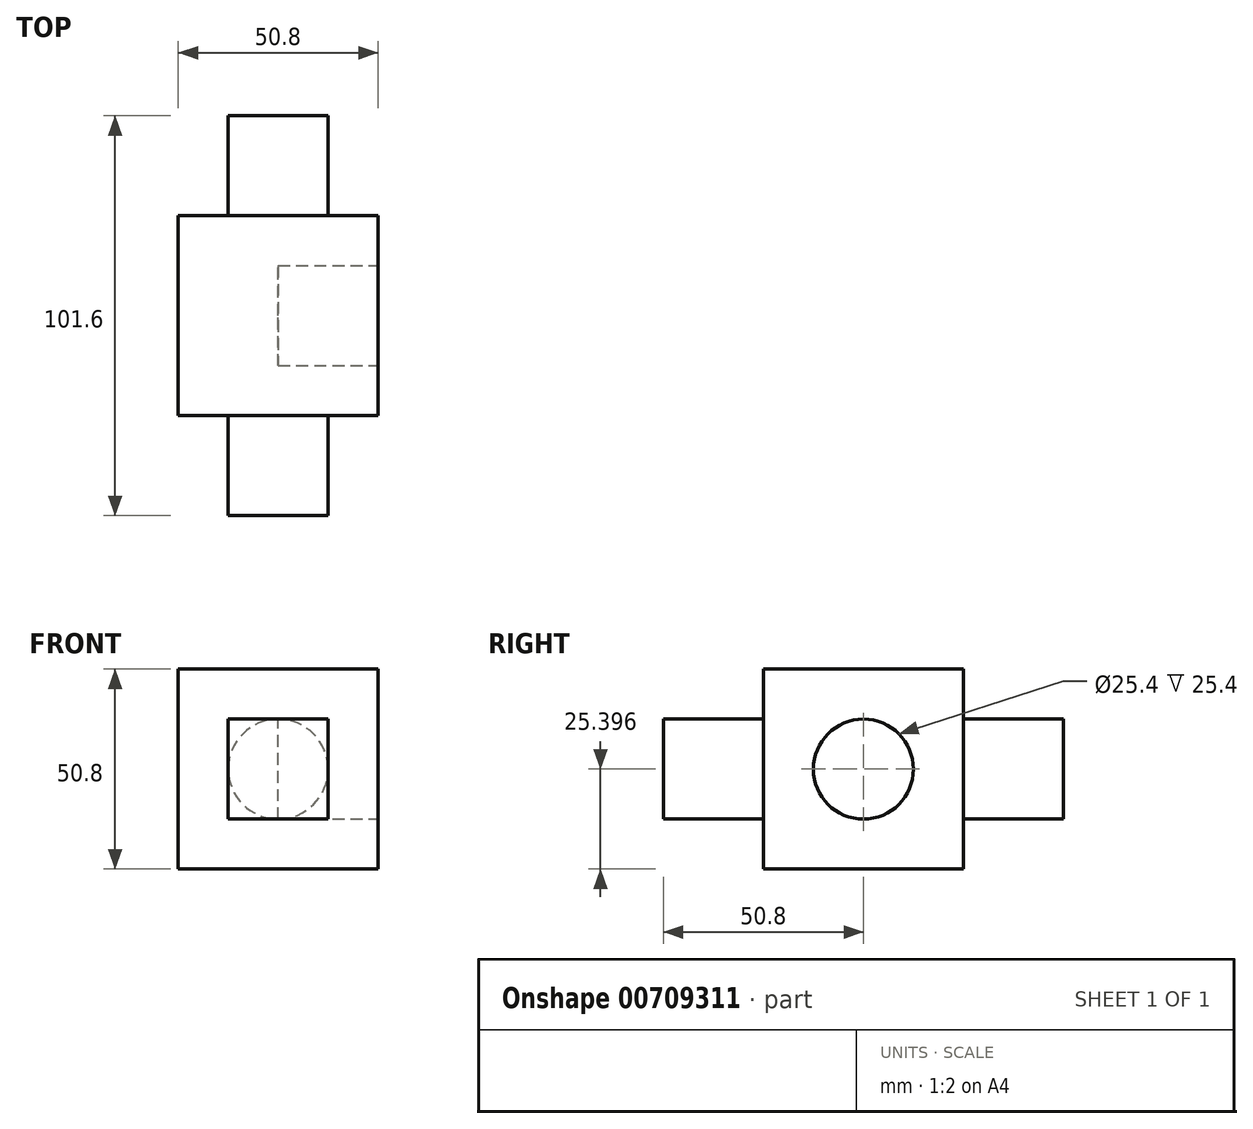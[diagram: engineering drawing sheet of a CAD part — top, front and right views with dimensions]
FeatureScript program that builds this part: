
annotation { "Feature Type Name" : "Feature", "Feature Type Description" : "" }
export const myFeature = defineFeature(function(context is Context, id is Id, definition is map)
    precondition{}
    {
        {
            var Q0;
            Q0=qCreatedBy(makeId("Front.planeOp"),FACE);
            var sketch = newSketch(context, id + "F0", { "sketchPlane" : qUnion([Q0])});
            skLineSegment(sketch, "E0.bottom", {"start": v(-56.81, 48.29) * mm, "end": v(-6.01, 48.29) * mm});
            skLineSegment(sketch, "E0.top", {"start": v(-56.81, -2.51) * mm, "end": v(-6.01, -2.51) * mm});
            skLineSegment(sketch, "E0.left", {"start": v(-56.81, 48.29) * mm, "end": v(-56.81, -2.51) * mm});
            skLineSegment(sketch, "E0.right", {"start": v(-6.01, 48.29) * mm, "end": v(-6.01, -2.51) * mm});
            skSolve(sketch);
        }
        {
            var Q0;
            Q0 = qSketchRegion(id + "F0", true);
            extrude(context, id + "F1", {"entities" : qUnion([Q0]), "depth" : 50.8 * mm, "offsetDistance" : 25.4 * mm});
        }
        {
            var Q0;
            Q0=makeQuery(id+"F1.opExtrude","CAP_FACE",FACE,{"disambiguationData":[OSD([sQuery(id+"F0.wireOp",EDGE,"E0.bottom"),sQuery(id+"F0.wireOp",EDGE,"E0.top"),sQuery(id+"F0.wireOp",EDGE,"E0.left"),sQuery(id+"F0.wireOp",EDGE,"E0.right")])],"isStart":false});
            var sketch = newSketch(context, id + "F2", { "sketchPlane" : qUnion([Q0])});
            skLineSegment(sketch, "E1.bottom", {"start": v(-44.11, 35.59) * mm, "end": v(-18.71, 35.59) * mm});
            skLineSegment(sketch, "E1.top", {"start": v(-44.11, 10.19) * mm, "end": v(-18.71, 10.19) * mm});
            skLineSegment(sketch, "E1.left", {"start": v(-44.11, 35.59) * mm, "end": v(-44.11, 10.19) * mm});
            skLineSegment(sketch, "E1.right", {"start": v(-18.71, 35.59) * mm, "end": v(-18.71, 10.19) * mm});
            skSolve(sketch);
        }
        {
            var Q0;
            Q0 = qSketchRegion(id + "F2", true);
            extrude(context, id + "F3", {"entities" : qUnion([Q0]), "operationType" : NewBodyOperationType.ADD, "depth" : 25.4 * mm, "offsetDistance" : 25.4 * mm});
        }
        {
            var Q0;
            Q0=makeQuery(id+"F1.opExtrude","SWEPT_FACE",FACE,{"disambiguationData":[OSD([sQuery(id+"F0.wireOp",EDGE,"E0.right")])]});
            var sketch = newSketch(context, id + "F4", { "sketchPlane" : qUnion([Q0])});
            skCircle(sketch, "E2", {"center": v(-25.4, 22.89) * mm, "radius": 12.7 * mm});
            skSolve(sketch);
        }
        {
            var Q0;
            Q0 = qSketchRegion(id + "F4", true);
            extrude(context, id + "F5", {"entities" : qUnion([Q0]), "operationType" : NewBodyOperationType.REMOVE, "oppositeDirection" : true, "depth" : 25.4 * mm, "offsetDistance" : 25.4 * mm});
        }
        {
            var Q0;
            Q0=makeQuery(id+"F1.opExtrude","CAP_FACE",FACE,{"disambiguationData":[OSD([sQuery(id+"F0.wireOp",EDGE,"E0.bottom"),sQuery(id+"F0.wireOp",EDGE,"E0.top"),sQuery(id+"F0.wireOp",EDGE,"E0.left"),sQuery(id+"F0.wireOp",EDGE,"E0.right")])],"isStart":true});
            var sketch = newSketch(context, id + "F6", { "sketchPlane" : qUnion([Q0])});
            skCircle(sketch, "E3", {"center": v(31.41, 22.89) * mm, "radius": 12.7 * mm});
            skSolve(sketch);
        }
        {
            var Q0;
            Q0 = qSketchRegion(id + "F6", true);
            extrude(context, id + "F7", {"entities" : qUnion([Q0]), "operationType" : NewBodyOperationType.ADD, "depth" : 25.4 * mm, "offsetDistance" : 25.4 * mm});
        }
    });
